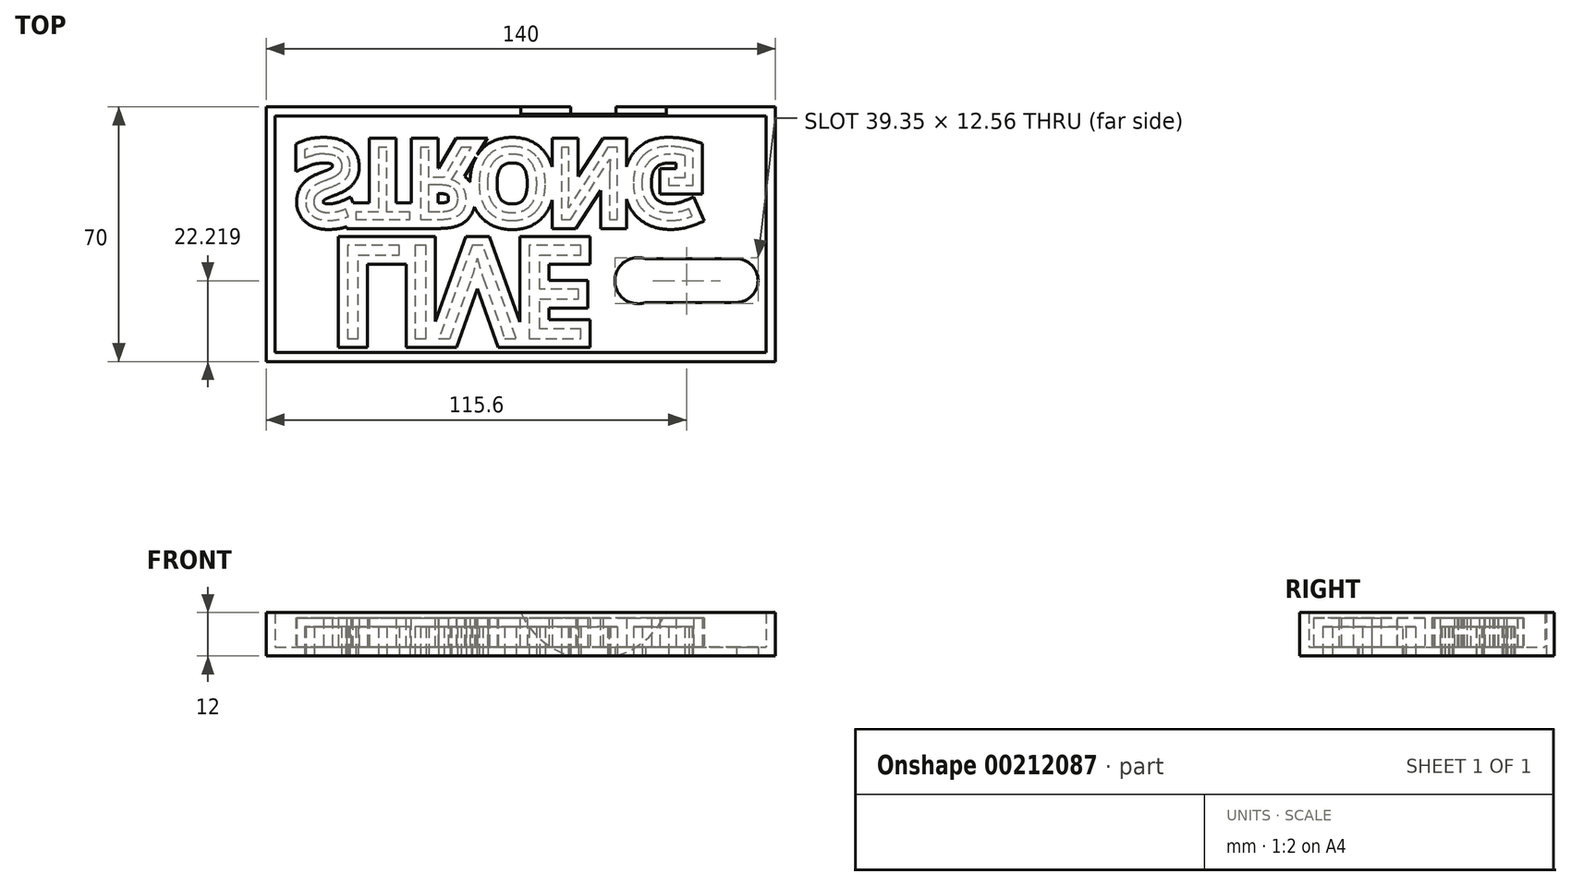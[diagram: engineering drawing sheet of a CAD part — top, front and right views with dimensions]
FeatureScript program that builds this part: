
annotation { "Feature Type Name" : "Feature", "Feature Type Description" : "" }
export const myFeature = defineFeature(function(context is Context, id is Id, definition is map)
    precondition{}
    {
        {
            var Q0;
            Q0=qCreatedBy(makeId("Top.planeOp"),FACE);
            var sketch = newSketch(context, id + "F0", { "sketchPlane" : qUnion([Q0])});
            skLineSegment(sketch, "E0.bottom", {"start": v(0, 0) * mm, "end": v(140, 0) * mm});
            skLineSegment(sketch, "E0.top", {"start": v(0, 70) * mm, "end": v(140, 70) * mm});
            skLineSegment(sketch, "E0.left", {"start": v(0, 0) * mm, "end": v(0, 70) * mm});
            skLineSegment(sketch, "E0.right", {"start": v(140, 0) * mm, "end": v(140, 70) * mm});
            skSolve(sketch);
        }
        {
            var Q0;
            Q0=makeQuery(id+"F0.imprint","IMPRINT",FACE,{"disambiguationData":[TD([[makeQuery(id+"F0.imprint","IMPRINT",EDGE,{"derivedFrom":sQuery(id+"F0.wireOp",EDGE,"E0.bottom")}),1.0]])]});
            extrude(context, id + "F1", {"entities" : qUnion([Q0]), "depth" : 12 * mm});
        }
        {
            var Q0;
            Q0=makeQuery(id+"F1.opExtrude","CAP_FACE",FACE,{"disambiguationData":[OSD([sQuery(id+"F0.wireOp",EDGE,"E0.bottom"),sQuery(id+"F0.wireOp",EDGE,"E0.top"),sQuery(id+"F0.wireOp",EDGE,"E0.left"),sQuery(id+"F0.wireOp",EDGE,"E0.right")])],"isStart":true});
            var sketch = newSketch(context, id + "F2", { "sketchPlane" : qUnion([Q0])});
            skText(sketch, "E1", { "text": "LIVE\n", "fontName": "OpenSans-Regular.ttf"});
            skText(sketch, "E2", { "text": "STRONG", "fontName": "OpenSans-Regular.ttf"});
            const initialGuessF2  = {"E1": [0.0189, -0.03193, 1, 0, 0.0258], "E2": [0.00923, -0.05886, 1, 0, 0.01994]};
            skSetInitialGuess(sketch, initialGuessF2);
            skSolve(sketch);
        }
        {
            var Q0;
            Q0 = qSketchRegion(id + "F2", true);
            extrude(context, id + "F3", {"entities" : qUnion([Q0]), "operationType" : NewBodyOperationType.REMOVE, "oppositeDirection" : true, "depth" : 8 * mm});
        }
        {
            var Q0;
            Q0=makeQuery(id+"F1.opExtrude","SWEPT_FACE",FACE,{"disambiguationData":[OSD([sQuery(id+"F0.wireOp",EDGE,"E0.top")])]});
            var sketch = newSketch(context, id + "F4", { "sketchPlane" : qUnion([Q0])});
            skLineSegment(sketch, "E3", {"start": v(-140, 12) * mm, "end": v(-110, 12) * mm});
            skLineSegment(sketch, "E4", {"start": v(0, 12) * mm, "end": v(-70, 12) * mm});
            skArc(sketch, "E5", {"start": v(-110, 12) * mm, "mid": v(-90, -0.91) * mm, "end": v(-70, 12) * mm});
            skSolve(sketch);
        }
        {
            var Q0;
            Q0=makeQuery(id+"F1.opExtrude","CAP_FACE",FACE,{"disambiguationData":[OSD([sQuery(id+"F0.wireOp",EDGE,"E0.bottom"),sQuery(id+"F0.wireOp",EDGE,"E0.top"),sQuery(id+"F0.wireOp",EDGE,"E0.left"),sQuery(id+"F0.wireOp",EDGE,"E0.right")])],"isStart":false});
            shell(context, id + "F5", {"entities" : qUnion([Q0]), "thickness" : 2.5 * mm});
        }
        {
            var Q0;
            {var subQ0=sQuery(id+"F4.wireOp",EDGE,"E5");var subQ1=sQuery(id+"F0.wireOp",EDGE,"E0.top");var subQ4=makeQuery(id+"F1.opExtrude","CAP_EDGE",EDGE,{"disambiguationData":[OSD([subQ1])],"isStart":true});var subQ5=makeQuery(id+"F4.imprint","INTERSECT",VERTEX,{"disambiguationData":[OD(0.0)],"derivedFrom":[subQ4,subQ0]});Q0=makeQuery(id+"F4.imprint","IMPRINT",FACE,{"disambiguationData":[TD([[makeQuery(id+"F4.imprint","IMPRINT",EDGE,{"disambiguationData":[TD([[subQ5,1.0]])],"derivedFrom":subQ4}),-1.0]])]});}
            extrude(context, id + "F6", {"entities" : qUnion([Q0]), "operationType" : NewBodyOperationType.REMOVE, "oppositeDirection" : true, "depth" : 2 * mm});
        }
        {
            var Q0;
            {var subQ0=sQuery(id+"F0.wireOp",EDGE,"E0.left");var subQ1=sQuery(id+"F0.wireOp",EDGE,"E0.bottom");var subQ2=sQuery(id+"F0.wireOp",EDGE,"E0.right");var subQ3=sQuery(id+"F0.wireOp",EDGE,"E0.top");Q0=makeQuery(id+"F3.boolean.opBoolean","SPLIT",FACE,{"disambiguationData":[TD([makeQuery(id+"F1.opExtrude","SWEPT_FACE",FACE,{"disambiguationData":[OSD([subQ1])]})])],"derivedFrom":makeQuery(id+"F1.opExtrude","CAP_FACE",FACE,{"disambiguationData":[OSD([subQ1,subQ3,subQ0,subQ2])],"isStart":true})});}
            var sketch = newSketch(context, id + "F7", { "sketchPlane" : qUnion([Q0])});
            skLineSegment(sketch, "E6.top", {"start": v(129.27, -28.25) * mm, "end": v(104.27, -28.25) * mm});
            skArc(sketch, "E7", {"start": v(129.27, -28.25) * mm, "mid": v(135.27, -22.3) * mm, "end": v(129.37, -16.25) * mm});
            skArc(sketch, "E8", {"start": v(104.37, -16.23) * mm, "mid": v(95.92, -22.18) * mm, "end": v(104.27, -28.25) * mm});
            skLineSegment(sketch, "E9", {"start": v(104.37, -16.23) * mm, "end": v(129.37, -16.25) * mm});
            skSolve(sketch);
        }
        {
            var Q0;
            Q0 = qSketchRegion(id + "F7", true);
            var Q1;
            Q1=sQuery(id+"F7.wireOp",EDGE,"E9");
            var Q2;
            Q2=sQuery(id+"F7.wireOp",EDGE,"E6.top");
            var Q3;
            Q3=sQuery(id+"F7.wireOp",EDGE,"E7");
            var Q4;
            Q4=sQuery(id+"F7.wireOp",EDGE,"E8");
            extrude(context, id + "F8", {"entities" : qUnion([Q0]), "operationType" : NewBodyOperationType.REMOVE, "surfaceEntities" : qUnion([Q1, Q2, Q3, Q4]), "oppositeDirection" : true, "depth" : 25 * mm});
        }
    });
